FCSTD DOCUMENT  (FreeCAD 1.0R39109 (Git))
Label: 30_shelf_base_assembly
License: All rights reserved
LicenseURL: http://en.wikipedia.org/wiki/All_rights_reserved
objects: App::FeaturePython×13, TechDraw::DrawViewDimension×7, App::Link×5, TechDraw::DrawProjGroupItem×5, Assembly::JointGroup×1, Assembly::AssemblyObject×1, TechDraw::DrawSVGTemplate×1, TechDraw::DrawProjGroup×1, TechDraw::DrawPage×1
note: 11 computed .brp shape members not serialized (recipe doc carries the construction recipe); baked Part::Feature solids carry a one-line shape summary decoded from their .brp
EXTERNAL_REF file=31_shelf_base_long.FCStd obj=Body
EXTERNAL_REF file=32_shelf_base_short.FCStd obj=Body

FEATURE [App::Link] Body
  LinkPlacement = pos=(0,0,0) rot=(1,0,0;3.14159rad)
  LinkedObject = -> <external 31_shelf_base_long.FCStd>#Body
  Placement = pos=(0,0,0) rot=(1,0,0;3.14159rad)
FEATURE [App::FeaturePython] GroundedJoint  # Assembly grounded joint (typed FeaturePython)
  ObjectToGround = -> Body
  Placement = pos=(0,0,0) rot=(1,0,0;3.14159rad)
FEATURE [App::Link] Body001
  LinkPlacement = pos=(-597,2.37e-14,69.5) rot=(-0.707107,0,0.707107;3.14159rad)
  LinkedObject = -> <external 32_shelf_base_short.FCStd>#Body
  Placement = pos=(-597,2.37e-14,69.5) rot=(-0.707107,0,0.707107;3.14159rad)
FEATURE [App::Link] Body002
  LinkPlacement = pos=(9,2.88e-14,69.5) rot=(0,-1,0;1.5708rad)
  LinkedObject = -> <external 32_shelf_base_short.FCStd>#Body
  Placement = pos=(9,2.88e-14,69.5) rot=(0,-1,0;1.5708rad)
FEATURE [App::Link] Body003
  LinkPlacement = pos=(597,6.5e-15,69.5) rot=(0,1,0;1.5708rad)
  LinkedObject = -> <external 32_shelf_base_short.FCStd>#Body
  Placement = pos=(597,6.5e-15,69.5) rot=(0,1,0;1.5708rad)
FEATURE [App::Link] Body004
  LinkPlacement = pos=(-4.74e-14,-1.168e-13,157) rot=(0,1,0;3.14159rad)
  LinkedObject = -> <external 31_shelf_base_long.FCStd>#Body
  Placement = pos=(-4.74e-14,-1.168e-13,157) rot=(0,1,0;3.14159rad)
FEATURE [App::FeaturePython] Joint  label="Distance"  # Assembly joint (typed FeaturePython)
  Activated = true
  AngleMax = 0
  AngleMin = 0
  Detach1 = false
  Detach2 = false
  Distance = 0
  Distance2 = 0
  EnableAngleMax = false
  EnableAngleMin = false
  EnableLengthMax = false
  EnableLengthMin = false
  JointType = 5 (Distance)
  LengthMax = 0
  LengthMin = 0
  Placement1 = pos=(-4e-15,1.1e-15,0) rot=(0,0,1;0rad)
  Placement2 = pos=(69.5,9e-16,9) rot=(-0.57735,0.57735,-0.57735;2.0944rad)
  Reference1 = -> Assembly [Body.Face5,Body.Vertex7]
  Reference2 = -> Assembly [Body001.Face2,Body001.Vertex5]
FEATURE [App::FeaturePython] Joint001  label="Distance001"  # Assembly joint (typed FeaturePython)
  Activated = true
  AngleMax = 0
  AngleMin = 0
  Detach1 = false
  Detach2 = false
  Distance = 0
  Distance2 = 0
  EnableAngleMax = false
  EnableAngleMin = false
  EnableLengthMax = false
  EnableLengthMin = false
  JointType = 5 (Distance)
  LengthMax = 0
  LengthMin = 0
  Placement1 = pos=(6.2e-15,100,9) rot=(-1,0,0;1.5708rad)
  Placement2 = pos=(0,100,9) rot=(-1,0,0;1.5708rad)
  Reference1 = -> Assembly [Body.Face1,Body.Vertex2]
  Reference2 = -> Assembly [Body001.Face1,Body001.Face1]
FEATURE [App::FeaturePython] Joint002  label="Distance002"  # Assembly joint (typed FeaturePython)
  Activated = true
  AngleMax = 0
  AngleMin = 0
  Detach1 = false
  Detach2 = false
  Distance = 0
  Distance2 = 0
  EnableAngleMax = false
  EnableAngleMin = false
  EnableLengthMax = false
  EnableLengthMin = false
  JointType = 5 (Distance)
  LengthMax = 0
  LengthMin = 0
  Placement1 = pos=(-615,-2.7e-15,9) rot=(-0.57735,-0.57735,0.57735;2.0944rad)
  Placement2 = pos=(-1.42e-14,5e-16,18) rot=(0,0,1;0rad)
  Reference1 = -> Assembly [Body.Face4,Body.Face4]
  Reference2 = -> Assembly [Body001.Face6,Body001.Face6]
FEATURE [App::FeaturePython] Joint003  label="Distance003"  # Assembly joint (typed FeaturePython)
  Activated = true
  AngleMax = 0
  AngleMin = 0
  Detach1 = false
  Detach2 = false
  Distance = 0
  Distance2 = 0
  EnableAngleMax = false
  EnableAngleMin = false
  EnableLengthMax = false
  EnableLengthMin = false
  JointType = 5 (Distance)
  LengthMax = 0
  LengthMin = 0
  Placement1 = pos=(0,-100,9) rot=(0,-0.707107,0.707107;3.14159rad)
  Placement2 = pos=(6.2e-15,100,9) rot=(-1,0,0;1.5708rad)
  Reference1 = -> Assembly [Body002.Face3,Body002.Face3]
  Reference2 = -> Assembly [Body.Face1,Body.Vertex2]
FEATURE [App::FeaturePython] Joint004  label="Distance004"  # Assembly joint (typed FeaturePython)
  Activated = true
  AngleMax = 0
  AngleMin = 0
  Detach1 = false
  Detach2 = false
  Distance = 0
  Distance2 = 0
  EnableAngleMax = false
  EnableAngleMin = false
  EnableLengthMax = false
  EnableLengthMin = false
  JointType = 5 (Distance)
  LengthMax = 0
  LengthMin = 0
  Placement1 = pos=(-69.5,0,9) rot=(-0.57735,-0.57735,0.57735;2.0944rad)
  Placement2 = pos=(-4e-15,1.1e-15,0) rot=(0,0,1;0rad)
  Reference1 = -> Assembly [Body002.Face4,Body002.Face4]
  Reference2 = -> Assembly [Body.Face5,Body.Vertex7]
FEATURE [App::FeaturePython] Joint005  label="Distance005"  # Assembly joint (typed FeaturePython)
  Activated = true
  AngleMax = 0
  AngleMin = 0
  Detach1 = false
  Detach2 = false
  Distance = -588
  Distance2 = 0
  EnableAngleMax = false
  EnableAngleMin = false
  EnableLengthMax = false
  EnableLengthMin = false
  JointType = 5 (Distance)
  LengthMax = 0
  LengthMin = 0
  Placement1 = pos=(0,2e-15,0) rot=(0,0,1;0rad)
  Placement2 = pos=(0,3.8e-15,18) rot=(0,0,1;0rad)
  Reference1 = -> Assembly [Body001.Face5,Body001.Face5]
  Reference2 = -> Assembly [Body002.Face6,Body002.Face6]
FEATURE [App::FeaturePython] Joint006  label="Distance006"  # Assembly joint (typed FeaturePython)
  Activated = true
  AngleMax = 0
  AngleMin = 0
  Detach1 = false
  Detach2 = false
  Distance = 0
  Distance2 = 0
  EnableAngleMax = false
  EnableAngleMin = false
  EnableLengthMax = false
  EnableLengthMin = false
  JointType = 5 (Distance)
  LengthMax = 0
  LengthMin = 0
  Placement1 = pos=(69.5,-4e-16,9) rot=(-0.57735,0.57735,-0.57735;2.0944rad)
  Placement2 = pos=(-4e-15,1.1e-15,0) rot=(0,0,1;0rad)
  Reference1 = -> Assembly [Body003.Face2,Body003.Face2]
  Reference2 = -> Assembly [Body.Face5,Body.Vertex3]
FEATURE [App::FeaturePython] Joint007  label="Distance007"  # Assembly joint (typed FeaturePython)
  Activated = true
  AngleMax = 0
  AngleMin = 0
  Detach1 = false
  Detach2 = false
  Distance = 0
  Distance2 = 0
  EnableAngleMax = false
  EnableAngleMin = false
  EnableLengthMax = false
  EnableLengthMin = false
  JointType = 5 (Distance)
  LengthMax = 0
  LengthMin = 0
  Placement1 = pos=(0,-100,9) rot=(0,-0.707107,0.707107;3.14159rad)
  Placement2 = pos=(6.2e-15,100,9) rot=(-1,0,0;1.5708rad)
  Reference1 = -> Assembly [Body003.Face3,Body003.Face3]
  Reference2 = -> Assembly [Body.Face1,Body.Face1]
FEATURE [App::FeaturePython] Joint008  label="Distance008"  # Assembly joint (typed FeaturePython)
  Activated = true
  AngleMax = 0
  AngleMin = 0
  Detach1 = false
  Detach2 = false
  Distance = 0
  Distance2 = 0
  EnableAngleMax = false
  EnableAngleMin = false
  EnableLengthMax = false
  EnableLengthMin = false
  JointType = 5 (Distance)
  LengthMax = 0
  LengthMin = 0
  Placement1 = pos=(-1.42e-14,1.1e-15,18) rot=(0,0,1;0rad)
  Placement2 = pos=(615,8e-16,9) rot=(-0.57735,0.57735,-0.57735;2.0944rad)
  Reference1 = -> Assembly [Body003.Face6,Body003.Vertex6]
  Reference2 = -> Assembly [Body.Face2,Body.Vertex4]
FEATURE [App::FeaturePython] Joint009  label="Distance009"  # Assembly joint (typed FeaturePython)
  Activated = true
  AngleMax = 0
  AngleMin = 0
  Detach1 = false
  Detach2 = false
  Distance = 0
  Distance2 = 0
  EnableAngleMax = false
  EnableAngleMin = false
  EnableLengthMax = false
  EnableLengthMin = false
  JointType = 5 (Distance)
  LengthMax = 0
  LengthMin = 0
  Placement1 = pos=(1.43e-14,3.6e-15,18) rot=(0,0,1;0rad)
  Placement2 = pos=(-69.5,-4e-16,9) rot=(-0.57735,-0.57735,0.57735;2.0944rad)
  Reference1 = -> Assembly [Body004.Face6,Body004.Face6]
  Reference2 = -> Assembly [Body003.Face4,Body003.Face4]
FEATURE [App::FeaturePython] Joint010  label="Distance010"  # Assembly joint (typed FeaturePython)
  Activated = true
  AngleMax = 0
  AngleMin = 0
  Detach1 = false
  Detach2 = false
  Distance = 0
  Distance2 = 0
  EnableAngleMax = false
  EnableAngleMin = false
  EnableLengthMax = false
  EnableLengthMin = false
  JointType = 5 (Distance)
  LengthMax = 0
  LengthMin = 0
  Placement1 = pos=(-615,-2.7e-15,9) rot=(-0.57735,-0.57735,0.57735;2.0944rad)
  Placement2 = pos=(-1.42e-14,1.1e-15,18) rot=(0,0,1;0rad)
  Reference1 = -> Assembly [Body004.Face4,Body004.Face4]
  Reference2 = -> Assembly [Body003.Face6,Body003.Face6]
FEATURE [App::FeaturePython] Joint011  label="Distance011"  # Assembly joint (typed FeaturePython)
  Activated = true
  AngleMax = 0
  AngleMin = 0
  Detach1 = false
  Detach2 = false
  Distance = 0
  Distance2 = 0
  EnableAngleMax = false
  EnableAngleMin = false
  EnableLengthMax = false
  EnableLengthMin = false
  JointType = 5 (Distance)
  LengthMax = 0
  LengthMin = 0
  Placement1 = pos=(-5e-15,-100,9) rot=(0,-0.707107,0.707107;3.14159rad)
  Placement2 = pos=(0,-100,9) rot=(0,-0.707107,0.707107;3.14159rad)
  Reference1 = -> Assembly [Body004.Face3,Body004.Vertex8]
  Reference2 = -> Assembly [Body003.Face3,Body003.Vertex7]
FEATURE [Assembly::JointGroup] Joints
  Group = -> [GroundedJoint,Joint,Joint001,Joint002,Joint003,Joint004,Joint005,Joint006,Joint007,Joint008,Joint009,Joint010,Joint011]
FEATURE [Assembly::AssemblyObject] Assembly
  Group = -> [Joints,Body,GroundedJoint,Body001,Body002,Body003,Body004,Joint,Joint001,Joint002,Joint003,Joint004,Joint005,Joint006,Joint007,Joint008,Joint009,Joint010,Joint011]
  Origin = -> Origin
  Type = Assembly
FEATURE [TechDraw::DrawSVGTemplate] Template
  EditableTexts = AuthorName=Matthias Mosimann; CheckDate=CHECK DATE; CreationDate=21/07/2025; DrawingNumber=NUMBER; FC-Scale=1 : 10; FC-Title=30_shelf_base_assembly; SheetNumber=2 / 2; Subtitle=Alle Dicken 18mm Buch keilverzinkt; SupervisorName=SUPERVISOR NAME; Weight=N/A
  Height = 297
  Orientation = 1
  Template = C:/Program Files/FreeCAD 1.0/data/Mod/TechDraw/Templates/A3_Landscape_TD.svg
  Width = 420
FEATURE [TechDraw::DrawProjGroupItem] View  label="Front"
  CoarseView = false
  Direction = (0,0,-1)
  Focus = 100
  HardHidden = false
  IsoCount = 0
  IsoHidden = false
  IsoVisible = false
  LockPosition = true
  Perspective = false
  Rotation = 0
  RotationVector = (1,0,0)
  Scale = 0.1
  ScaleType = 2
  ScrubCount = 1
  SeamHidden = false
  SeamVisible = true
  SmoothHidden = false
  SmoothVisible = true
  Source = -> [Assembly]
  Type = 0
  X = 0
  XDirection = (1,0,0)
  Y = 0
FEATURE [TechDraw::DrawProjGroupItem] ProjItem  label="Right"
  CoarseView = false
  Direction = (1,0,-1e-16)
  Focus = 100
  HardHidden = false
  IsoCount = 0
  IsoHidden = false
  IsoVisible = false
  LockPosition = false
  Perspective = false
  Rotation = 0
  RotationVector = (1,0,0)
  ScaleType = 0
  ScrubCount = 1
  SeamHidden = false
  SeamVisible = true
  SmoothHidden = false
  SmoothVisible = true
  Source = -> [Assembly]
  Type = 2
  X = -97.1751
  XDirection = (1e-16,0,1)
  Y = 0
FEATURE [TechDraw::DrawProjGroupItem] ProjItem001  label="Left"
  CoarseView = false
  Direction = (-1,0,-1e-16)
  Focus = 100
  HardHidden = false
  IsoCount = 0
  IsoHidden = false
  IsoVisible = false
  LockPosition = false
  Perspective = false
  Rotation = 0
  RotationVector = (1,0,0)
  ScaleType = 0
  ScrubCount = 1
  SeamHidden = false
  SeamVisible = true
  SmoothHidden = false
  SmoothVisible = true
  Source = -> [Assembly]
  Type = 1
  X = 87.4057
  XDirection = (1e-16,0,-1)
  Y = 0
FEATURE [TechDraw::DrawProjGroupItem] ProjItem002  label="Bottom"
  CoarseView = false
  Direction = (0,1,0)
  Focus = 100
  HardHidden = false
  IsoCount = 0
  IsoHidden = false
  IsoVisible = false
  LockPosition = false
  Perspective = false
  Rotation = 0
  RotationVector = (1,0,0)
  ScaleType = 0
  ScrubCount = 1
  SeamHidden = false
  SeamVisible = true
  SmoothHidden = false
  SmoothVisible = true
  Source = -> [Assembly]
  Type = 5
  X = 0
  XDirection = (1,0,0)
  Y = 40.9051
FEATURE [TechDraw::DrawProjGroup] ProjGroup
  Anchor = -> View
  AutoDistribute = false
  LockPosition = false
  ProjectionType = 0
  Rotation = 0
  Scale = 0.1
  ScaleType = 2
  Source = -> [Assembly]
  Views = -> [View,ProjItem,ProjItem001,ProjItem002]
  X = 167.384
  Y = 192.741
  spacingX = 25
  spacingY = 25
FEATURE [TechDraw::DrawViewDimension] Dimension
  AngleOverride = false
  Arbitrary = false
  ArbitraryTolerances = false
  BoxCorners = (2) [(-61.5,-8.75,0),(61.5,8.75,0)]
  EqualTolerance = true
  ExtensionAngle = 0
  FormatSpec = %.2w
  FormatSpecOverTolerance = %+.2w
  FormatSpecUnderTolerance = %+.2w
  Inverted = false
  LineAngle = 0
  LockPosition = false
  MeasureType = 1
  OverTolerance = 0
  References2D = -> [ProjItem002]
  Rotation = 0
  ScaleType = 0
  TheoreticalExact = false
  Type = 1
  UnderTolerance = 0
  X = 0
  Y = 25.6778
FEATURE [TechDraw::DrawViewDimension] Dimension001
  AngleOverride = false
  Arbitrary = false
  ArbitraryTolerances = false
  BoxCorners = (2) [(-61.5,-8.75,0),(61.5,8.75,0)]
  EqualTolerance = true
  ExtensionAngle = 0
  FormatSpec = %.2w
  FormatSpecOverTolerance = %+.2w
  FormatSpecUnderTolerance = %+.2w
  Inverted = false
  LineAngle = 0
  LockPosition = false
  MeasureType = 1
  OverTolerance = 0
  References2D = -> [ProjItem002]
  Rotation = 0
  ScaleType = 0
  TheoreticalExact = false
  Type = 0
  UnderTolerance = 0
  X = -82.7399
  Y = -3.53099
FEATURE [TechDraw::DrawViewDimension] Dimension002
  AngleOverride = false
  Arbitrary = false
  ArbitraryTolerances = false
  BoxCorners = (2) [(-8.75,-10,0),(8.75,10,0)]
  EqualTolerance = true
  ExtensionAngle = 0
  FormatSpec = %.2w
  FormatSpecOverTolerance = %+.2w
  FormatSpecUnderTolerance = %+.2w
  Inverted = false
  LineAngle = 0
  LockPosition = false
  MeasureType = 1
  OverTolerance = 0
  References2D = -> [ProjItem]
  Rotation = 0
  ScaleType = 0
  TheoreticalExact = false
  Type = 1
  UnderTolerance = 0
  X = 0
  Y = 24.1589
FEATURE [TechDraw::DrawViewDimension] Dimension003
  AngleOverride = false
  Arbitrary = false
  ArbitraryTolerances = false
  BoxCorners = (2) [(-8.75,-10,0),(8.75,10,0)]
  EqualTolerance = true
  ExtensionAngle = 0
  FormatSpec = %.2w
  FormatSpecOverTolerance = %+.2w
  FormatSpecUnderTolerance = %+.2w
  Inverted = false
  LineAngle = 0
  LockPosition = false
  MeasureType = 1
  OverTolerance = 0
  References2D = -> [ProjItem]
  Rotation = 0
  ScaleType = 0
  TheoreticalExact = false
  Type = 2
  UnderTolerance = 0
  X = -19.9432
  Y = 19.9724
FEATURE [TechDraw::DrawViewDimension] Dimension004
  AngleOverride = false
  Arbitrary = false
  ArbitraryTolerances = false
  BoxCorners = (2) [(-61.5,-8.75,0),(61.5,8.75,0)]
  EqualTolerance = true
  ExtensionAngle = 0
  FormatSpec = %.2w
  FormatSpecOverTolerance = %+.2w
  FormatSpecUnderTolerance = %+.2w
  Inverted = false
  LineAngle = 0
  LockPosition = false
  MeasureType = 1
  OverTolerance = 0
  References2D = -> [ProjItem002]
  Rotation = 0
  ScaleType = 0
  TheoreticalExact = false
  Type = 0
  UnderTolerance = 0
  X = -35.2815
  Y = 18.6778
FEATURE [TechDraw::DrawViewDimension] Dimension005
  AngleOverride = false
  Arbitrary = false
  ArbitraryTolerances = false
  BoxCorners = (2) [(-61.5,-8.75,0),(61.5,8.75,0)]
  EqualTolerance = true
  ExtensionAngle = 0
  FormatSpec = %.2w
  FormatSpecOverTolerance = %+.2w
  FormatSpecUnderTolerance = %+.2w
  Inverted = false
  LineAngle = 0
  LockPosition = false
  MeasureType = 1
  OverTolerance = 0
  References2D = -> [ProjItem002]
  Rotation = 0
  ScaleType = 0
  TheoreticalExact = false
  Type = 0
  UnderTolerance = 0
  X = 30.3
  Y = 18.6778
FEATURE [TechDraw::DrawViewDimension] Dimension006
  AngleOverride = false
  Arbitrary = false
  ArbitraryTolerances = false
  BoxCorners = (2) [(-61.5,-8.75,0),(61.5,8.75,0)]
  EqualTolerance = true
  ExtensionAngle = 0
  FormatSpec = %.2w
  FormatSpecOverTolerance = %+.2w
  FormatSpecUnderTolerance = %+.2w
  Inverted = false
  LineAngle = 0
  LockPosition = false
  MeasureType = 1
  OverTolerance = 0
  References2D = -> [ProjItem002]
  Rotation = 0
  ScaleType = 0
  TheoreticalExact = false
  Type = 0
  UnderTolerance = 0
  X = -72.8372
  Y = -18.7999
FEATURE [TechDraw::DrawProjGroupItem] View001
  CoarseView = false
  Direction = (-0.57735,-0.57735,0.57735)
  Focus = 100
  HardHidden = false
  IsoCount = 0
  IsoHidden = false
  IsoVisible = false
  LockPosition = false
  Perspective = false
  Rotation = 0
  RotationVector = (1,0,0)
  Scale = 0.1
  ScaleType = 2
  ScrubCount = 1
  SeamHidden = false
  SeamVisible = true
  SmoothHidden = false
  SmoothVisible = true
  Source = -> [Assembly]
  Type = 0
  X = 332.244
  XDirection = (-0.707107,0,-0.707107)
  Y = 168.699
FEATURE [TechDraw::DrawPage] Page001
  KeepUpdated = true
  NextBalloonIndex = 1
  ProjectionType = 0
  Template = -> Template
  Views = -> [ProjGroup,Dimension,Dimension001,Dimension002,Dimension003,Dimension004,Dimension005,Dimension006,View001]

RESOLVED EXTERNAL PARTS (link-assembly join: the EXTERNAL_REF files above that resolve inside this repo's crawl, each included once):
---- part 31_shelf_base_long.FCStd = doc fcstd_5816eb6c3fd6 ----
FCSTD DOCUMENT  (FreeCAD 1.0R39109 (Git))
Label: 31_shelf_base_long
License: All rights reserved
LicenseURL: http://en.wikipedia.org/wiki/All_rights_reserved
objects: Spreadsheet::Sheet×1, Sketcher::SketchObject×1, PartDesign::Pad×1, PartDesign::Body×1
note: 6 computed .brp shape members not serialized (recipe doc carries the construction recipe); baked Part::Feature solids carry a one-line shape summary decoded from their .brp

FEATURE [Spreadsheet::Sheet] Spreadsheet
  cells = A2='length; B2(length)=1230; A3='width; B3(width)=200; A4='height; B4(height)=18
FEATURE [Sketcher::SketchObject] Sketch
  ArcFitTolerance = 0
  AttachmentSupport = -> [XY_Plane]
  FullyConstrained = true
  MakeInternals = false
  MapMode = 5
  expr: Constraints[11] = Spreadsheet.length
  expr: Constraints[12] = Spreadsheet.width
  sketch-geometry (5):
    g0: LineSegment StartX=-615 StartY=100 StartZ=0 EndX=615 EndY=100 EndZ=0
    g1: LineSegment StartX=615 StartY=100 StartZ=0 EndX=615 EndY=-100 EndZ=0
    g2: LineSegment StartX=615 StartY=-100 StartZ=0 EndX=-615 EndY=-100 EndZ=0
    g3: LineSegment StartX=-615 StartY=-100 StartZ=0 EndX=-615 EndY=100 EndZ=0
    g4: LineSegment [constr] StartX=-615 StartY=100 StartZ=0 EndX=615 EndY=-100 EndZ=0
  constraints (13):
    c: Coincident(g0,g1)
    c: Coincident(g1,g2)
    c: Coincident(g2,g3)
    c: Coincident(g3,g0)
    c: Horizontal(g0)
    c: Horizontal(g2)
    c: Vertical(g1)
    c: Vertical(g3)
    c: Coincident(g4,g1)
    c: Coincident(g0,g4)
    c: Symmetric(g0,g1,g-1)
    c: Distance(g0,g0) = 1230
    c: Distance(g0,g2) = 200
FEATURE [PartDesign::Pad] Pad
  Direction = (0,0,1)
  Length = 18
  Length2 = 10
  Profile = -> Sketch
  ReferenceAxis = -> Sketch [N_Axis]
  Suppressed = false
  Type = 0
  expr: Length = Spreadsheet.height
FEATURE [PartDesign::Body] Body
  AllowCompound = false
  Group = -> [Sketch,Pad]
  Origin = -> Origin
  Tip = -> Pad
---- part 32_shelf_base_short.FCStd = doc fcstd_6d521a47aa60 ----
FCSTD DOCUMENT  (FreeCAD 1.0R39109 (Git))
Label: 32_shelf_base_short
License: All rights reserved
LicenseURL: http://en.wikipedia.org/wiki/All_rights_reserved
objects: Spreadsheet::Sheet×1, Sketcher::SketchObject×1, PartDesign::Pad×1, PartDesign::Body×1
note: 6 computed .brp shape members not serialized (recipe doc carries the construction recipe); baked Part::Feature solids carry a one-line shape summary decoded from their .brp

FEATURE [Spreadsheet::Sheet] Spreadsheet
  cells = A2='length; B2(length)=139; A3='width; B3(width)=200; A4='height; B4(height)=18
FEATURE [Sketcher::SketchObject] Sketch
  ArcFitTolerance = 0
  AttachmentSupport = -> [XY_Plane]
  FullyConstrained = true
  MakeInternals = false
  MapMode = 5
  expr: Constraints[11] = Spreadsheet.length
  expr: Constraints[12] = Spreadsheet.width
  sketch-geometry (5):
    g0: LineSegment StartX=-69.5 StartY=100 StartZ=0 EndX=69.5 EndY=100 EndZ=0
    g1: LineSegment StartX=69.5 StartY=100 StartZ=0 EndX=69.5 EndY=-100 EndZ=0
    g2: LineSegment StartX=69.5 StartY=-100 StartZ=0 EndX=-69.5 EndY=-100 EndZ=0
    g3: LineSegment StartX=-69.5 StartY=-100 StartZ=0 EndX=-69.5 EndY=100 EndZ=0
    g4: LineSegment [constr] StartX=-69.5 StartY=100 StartZ=0 EndX=69.5 EndY=-100 EndZ=0
  constraints (13):
    c: Coincident(g0,g1)
    c: Coincident(g1,g2)
    c: Coincident(g2,g3)
    c: Coincident(g3,g0)
    c: Horizontal(g0)
    c: Horizontal(g2)
    c: Vertical(g1)
    c: Vertical(g3)
    c: Coincident(g4,g1)
    c: Coincident(g0,g4)
    c: Symmetric(g0,g1,g-1)
    c: Distance(g0,g0) = 139
    c: Distance(g0,g2) = 200
FEATURE [PartDesign::Pad] Pad
  Direction = (0,0,1)
  Length = 18
  Length2 = 10
  Profile = -> Sketch
  ReferenceAxis = -> Sketch [N_Axis]
  Suppressed = false
  Type = 0
  expr: Length = Spreadsheet.height
FEATURE [PartDesign::Body] Body
  AllowCompound = false
  Group = -> [Sketch,Pad]
  Origin = -> Origin
  Tip = -> Pad
